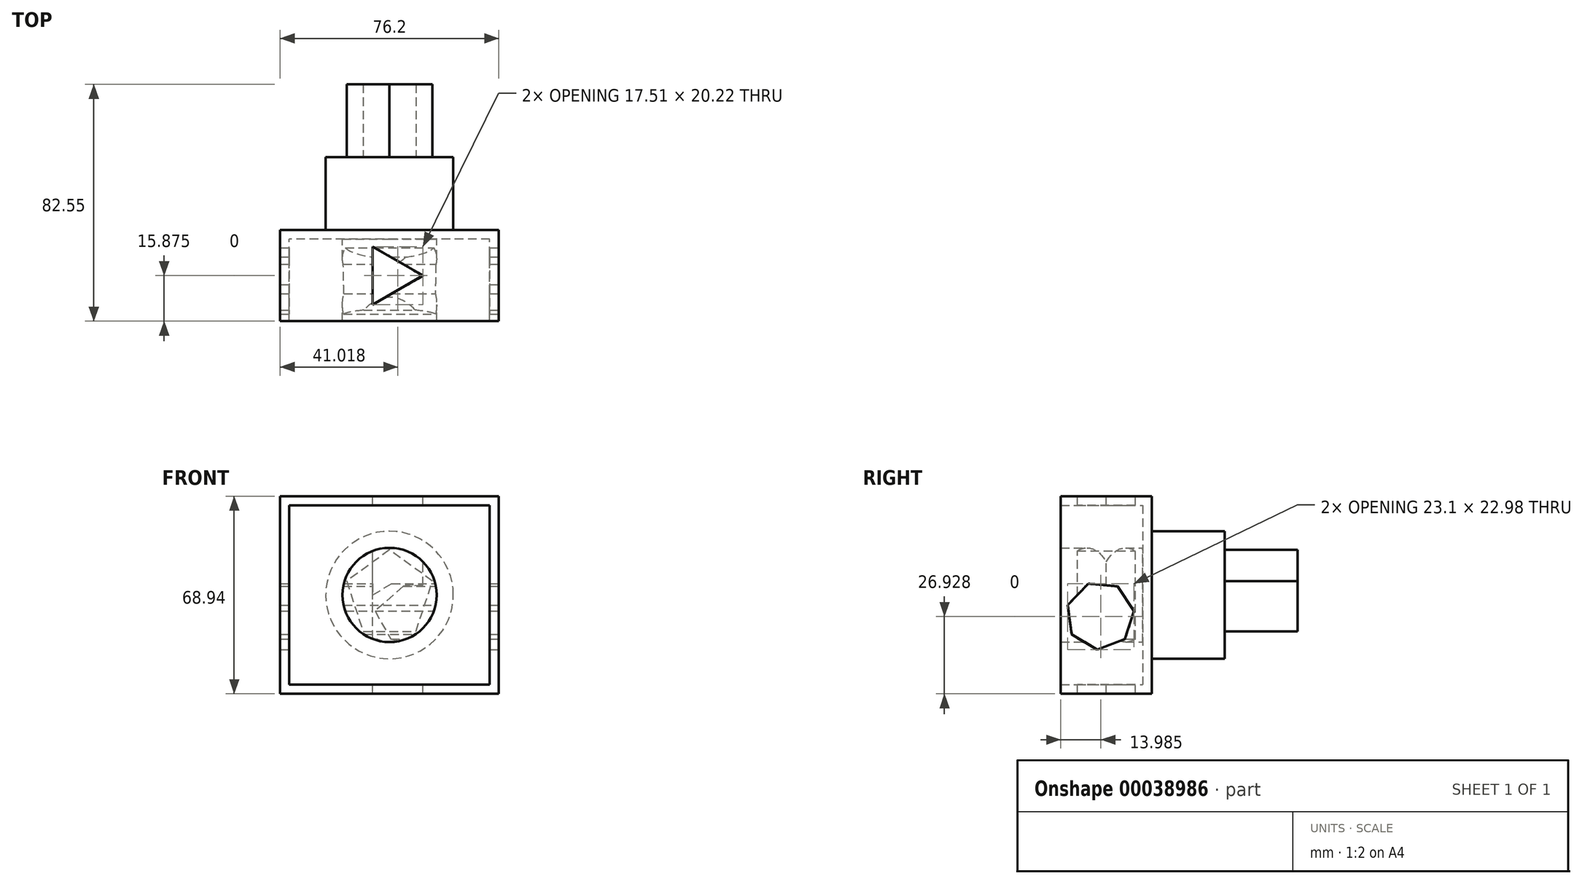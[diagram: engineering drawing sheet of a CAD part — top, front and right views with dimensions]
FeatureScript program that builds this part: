
annotation { "Feature Type Name" : "Feature", "Feature Type Description" : "" }
export const myFeature = defineFeature(function(context is Context, id is Id, definition is map)
    precondition{}
    {
        {
            var Q0;
            Q0=qCreatedBy(makeId("Front.planeOp"),FACE);
            var sketch = newSketch(context, id + "F0", { "sketchPlane" : qUnion([Q0])});
            skLineSegment(sketch, "E0.rect.bottom", {"start": v(38.1, 34.47) * mm, "end": v(-38.1, 34.47) * mm});
            skLineSegment(sketch, "E0.rect.top", {"start": v(38.1, -34.47) * mm, "end": v(-38.1, -34.47) * mm});
            skLineSegment(sketch, "E0.rect.left", {"start": v(38.1, 34.47) * mm, "end": v(38.1, -34.47) * mm});
            skLineSegment(sketch, "E0.rect.right", {"start": v(-38.1, 34.47) * mm, "end": v(-38.1, -34.47) * mm});
            skPoint(sketch, "E0.rect.middle", {"position": v(0, 0) * mm});
            skSolve(sketch);
        }
        {
            var Q0;
            Q0=makeQuery(id+"F0.imprint","IMPRINT",FACE,{"disambiguationData":[TD([[makeQuery(id+"F0.imprint","IMPRINT",EDGE,{"derivedFrom":sQuery(id+"F0.wireOp",EDGE,"E0.rect.bottom")}),1.0]])]});
            extrude(context, id + "F10", {"entities" : qUnion([Q0]), "depth" : 31.75 * mm});
        }
        {
            var Q0;
            Q0=makeQuery(id+"F10.opExtrude","CAP_FACE",FACE,{"disambiguationData":[OSD([sQuery(id+"F0.wireOp",EDGE,"E0.rect.bottom"),sQuery(id+"F0.wireOp",EDGE,"E0.rect.top"),sQuery(id+"F0.wireOp",EDGE,"E0.rect.left"),sQuery(id+"F0.wireOp",EDGE,"E0.rect.right")])],"isStart":false});
            shell(context, id + "F1", {"entities" : qUnion([Q0]), "thickness" : 3.17 * mm});
        }
        {
            var Q0;
            Q0=makeQuery(id+"F10.opExtrude","CAP_FACE",FACE,{"disambiguationData":[OSD([sQuery(id+"F0.wireOp",EDGE,"E0.rect.bottom"),sQuery(id+"F0.wireOp",EDGE,"E0.rect.top"),sQuery(id+"F0.wireOp",EDGE,"E0.rect.left"),sQuery(id+"F0.wireOp",EDGE,"E0.rect.right")])],"isStart":true});
            var sketch = newSketch(context, id + "F2", { "sketchPlane" : qUnion([Q0])});
            skCircle(sketch, "E1", {"center": v(0, 0) * mm, "radius": 22.23 * mm});
            skSolve(sketch);
        }
        {
            var Q0;
            Q0 = qSketchRegion(id + "F2", true);
            extrude(context, id + "F3", {"entities" : qUnion([Q0]), "operationType" : NewBodyOperationType.ADD, "depth" : 25.4 * mm});
        }
        {
            var Q0;
            Q0=makeQuery(id+"F3.opExtrude","CAP_FACE",FACE,{"disambiguationData":[OSD([sQuery(id+"F2.wireOp",EDGE,"E1")])],"isStart":false});
            var sketch = newSketch(context, id + "F4", { "sketchPlane" : qUnion([Q0])});
            skCircle(sketch, "E2.cCircle", {"center": v(0, 0) * mm, "radius": 12.7 * mm, "construction": true});
            skLineSegment(sketch, "E2.0", {"start": v(9.23, -12.7) * mm, "end": v(-9.23, -12.7) * mm});
            skLineSegment(sketch, "E2.1", {"start": v(-9.23, -12.7) * mm, "end": v(-14.93, 4.85) * mm});
            skLineSegment(sketch, "E2.2", {"start": v(-14.93, 4.85) * mm, "end": v(0, 15.7) * mm});
            skLineSegment(sketch, "E2.3", {"start": v(0, 15.7) * mm, "end": v(14.93, 4.85) * mm});
            skLineSegment(sketch, "E2.4", {"start": v(14.93, 4.85) * mm, "end": v(9.23, -12.7) * mm});
            skPoint(sketch, "E2.0.midPoint", {"position": v(0, -12.7) * mm});
            skSolve(sketch);
        }
        {
            var Q0;
            Q0=makeQuery(id+"F4.imprint","IMPRINT",FACE,{"disambiguationData":[TD([[makeQuery(id+"F4.imprint","IMPRINT",EDGE,{"derivedFrom":sQuery(id+"F4.wireOp",EDGE,"E2.0")}),-1.0]])]});
            extrude(context, id + "F5", {"entities" : qUnion([Q0]), "operationType" : NewBodyOperationType.ADD, "depth" : 25.4 * mm});
        }
        {
            var Q0;
            Q0=makeQuery(id+"F1.opShell","OFFSET_FACE",FACE,{"disambiguationData":[OSD([sQuery(id+"F0.wireOp",EDGE,"E0.rect.bottom"),sQuery(id+"F0.wireOp",EDGE,"E0.rect.top"),sQuery(id+"F0.wireOp",EDGE,"E0.rect.left"),sQuery(id+"F0.wireOp",EDGE,"E0.rect.right")])]});
            var sketch = newSketch(context, id + "F11", { "sketchPlane" : qUnion([Q0])});
            skCircle(sketch, "E3", {"center": v(0, 0) * mm, "radius": 16.42 * mm});
            skSolve(sketch);
        }
        {
            var Q0;
            Q0=makeQuery(id+"F11.imprint","IMPRINT",FACE,{"disambiguationData":[TD([[makeQuery(id+"F11.imprint","IMPRINT",EDGE,{"derivedFrom":sQuery(id+"F11.wireOp",EDGE,"E3")}),1.0]])]});
            var Q1;
            Q1=makeQuery(id+"F10.opExtrude","CAP_FACE",FACE,{"disambiguationData":[OSD([sQuery(id+"F0.wireOp",EDGE,"E0.rect.bottom"),sQuery(id+"F0.wireOp",EDGE,"E0.rect.top"),sQuery(id+"F0.wireOp",EDGE,"E0.rect.left"),sQuery(id+"F0.wireOp",EDGE,"E0.rect.right")])],"isStart":false});
            extrude(context, id + "F6", {"entities" : qUnion([Q0]), "operationType" : NewBodyOperationType.ADD, "endBound" : BoundingType.UP_TO_SURFACE, "endBoundEntityFace" : qUnion([Q1]), "depth" : 25.4 * mm});
        }
        {
            var Q0;
            Q0=makeQuery(id+"F10.opExtrude","SWEPT_FACE",FACE,{"disambiguationData":[OSD([sQuery(id+"F0.wireOp",EDGE,"E0.rect.left")])]});
            var sketch = newSketch(context, id + "F7", { "sketchPlane" : qUnion([Q0])});
            skCircle(sketch, "E4.cCircle", {"center": v(-18, -7.19) * mm, "radius": 10.72 * mm, "construction": true});
            skLineSegment(sketch, "E4.0", {"start": v(-19.07, -19.03) * mm, "end": v(-27.93, -13.74) * mm});
            skLineSegment(sketch, "E4.1", {"start": v(-27.93, -13.74) * mm, "end": v(-29.31, -3.51) * mm});
            skLineSegment(sketch, "E4.2", {"start": v(-29.31, -3.51) * mm, "end": v(-22.18, 3.95) * mm});
            skLineSegment(sketch, "E4.3", {"start": v(-22.18, 3.95) * mm, "end": v(-11.9, 3.02) * mm});
            skLineSegment(sketch, "E4.4", {"start": v(-11.9, 3.02) * mm, "end": v(-6.22, -5.59) * mm});
            skLineSegment(sketch, "E4.5", {"start": v(-6.22, -5.59) * mm, "end": v(-9.4, -15.4) * mm});
            skLineSegment(sketch, "E4.6", {"start": v(-9.4, -15.4) * mm, "end": v(-19.07, -19.03) * mm});
            skPoint(sketch, "E4.0.midPoint", {"position": v(-23.5, -16.39) * mm});
            skSolve(sketch);
        }
        {
            var Q0;
            Q0=makeQuery(id+"F7.imprint","IMPRINT",FACE,{"disambiguationData":[TD([[makeQuery(id+"F7.imprint","IMPRINT",EDGE,{"derivedFrom":sQuery(id+"F7.wireOp",EDGE,"E4.0")}),-1.0]])]});
            extrude(context, id + "F8", {"entities" : qUnion([Q0]), "operationType" : NewBodyOperationType.REMOVE, "endBound" : BoundingType.THROUGH_ALL, "oppositeDirection" : true, "depth" : 86 * mm});
        }
        {
            var Q0;
            Q0=makeQuery(id+"F10.opExtrude","SWEPT_FACE",FACE,{"disambiguationData":[OSD([sQuery(id+"F0.wireOp",EDGE,"E0.rect.bottom")])]});
            var sketch = newSketch(context, id + "F9", { "sketchPlane" : qUnion([Q0])});
            skLineSegment(sketch, "E5", {"start": v(0, -31.75) * mm, "end": v(0, 0) * mm, "construction": true});
            skCircle(sketch, "E6.cCircle", {"center": v(0, -15.88) * mm, "radius": 5.84 * mm, "construction": true});
            skLineSegment(sketch, "E6.0", {"start": v(-5.84, -25.98) * mm, "end": v(-5.84, -5.77) * mm});
            skLineSegment(sketch, "E6.1", {"start": v(-5.84, -5.77) * mm, "end": v(11.67, -15.88) * mm});
            skLineSegment(sketch, "E6.2", {"start": v(11.67, -15.88) * mm, "end": v(-5.84, -25.98) * mm});
            skPoint(sketch, "E6.0.midPoint", {"position": v(-5.84, -15.88) * mm});
            skSolve(sketch);
        }
        {
            var Q0;
            Q0 = qSketchRegion(id + "F9", true);
            extrude(context, id + "F12", {"entities" : qUnion([Q0]), "operationType" : NewBodyOperationType.REMOVE, "endBound" : BoundingType.THROUGH_ALL, "oppositeDirection" : true, "depth" : 25.4 * mm});
        }
    });
